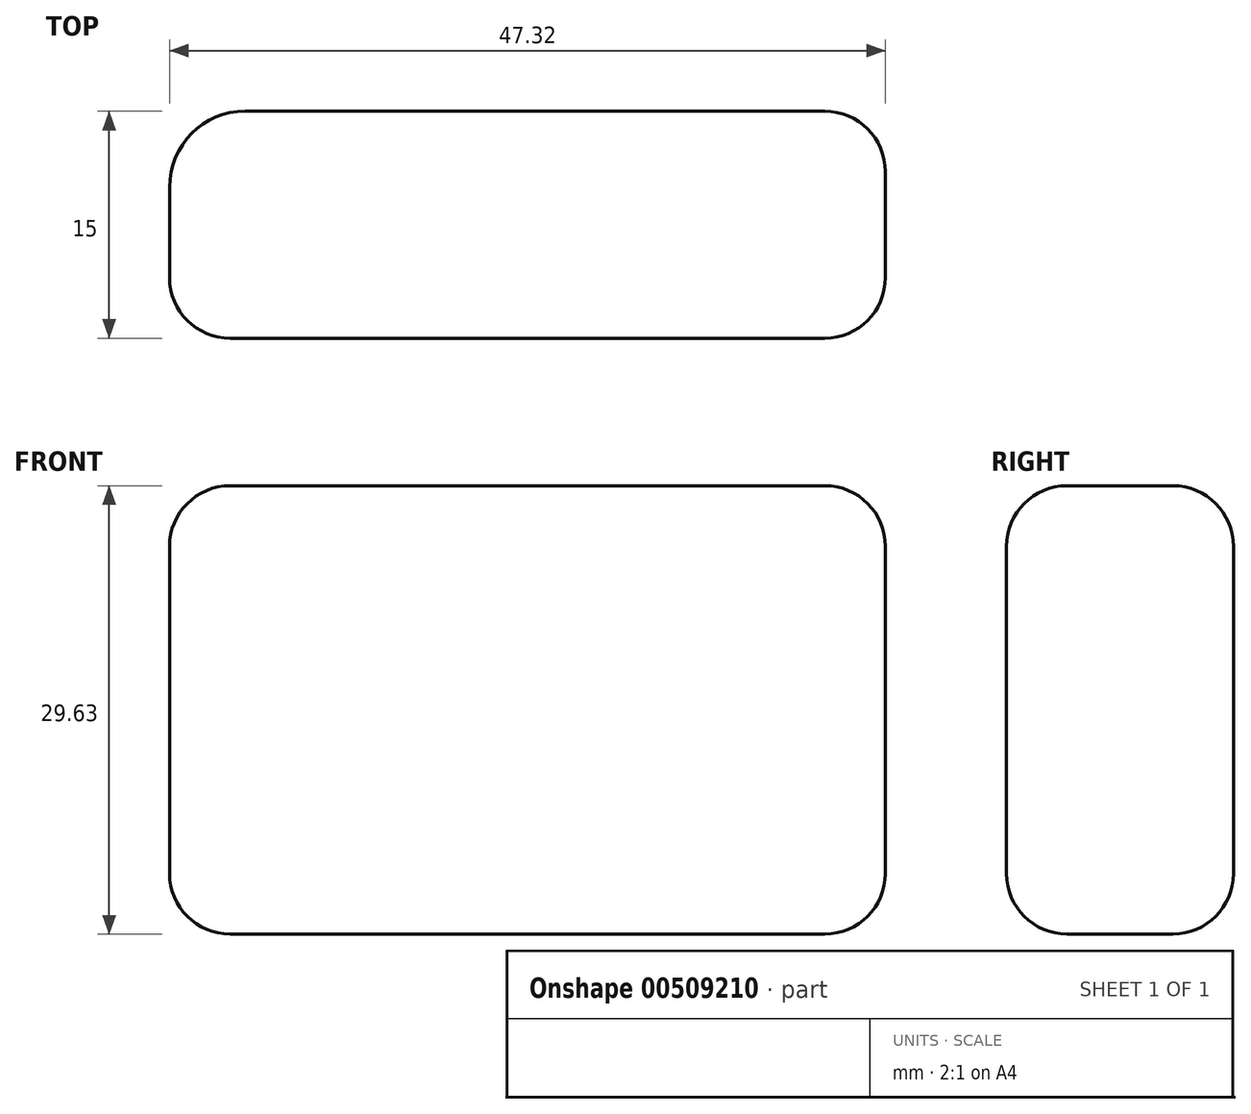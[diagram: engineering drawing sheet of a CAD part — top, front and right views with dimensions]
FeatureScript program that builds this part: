
annotation { "Feature Type Name" : "Feature", "Feature Type Description" : "" }
export const myFeature = defineFeature(function(context is Context, id is Id, definition is map)
    precondition{}
    {
        {
            var Q0;
            Q0=qCreatedBy(makeId("Front.planeOp"),FACE);
            var sketch = newSketch(context, id + "F0", { "sketchPlane" : qUnion([Q0])});
            skLineSegment(sketch, "E0.bottom", {"start": v(-65.84, 12.9) * mm, "end": v(-18.52, 12.9) * mm});
            skLineSegment(sketch, "E0.top", {"start": v(-65.84, -16.72) * mm, "end": v(-18.52, -16.72) * mm});
            skLineSegment(sketch, "E0.left", {"start": v(-65.84, 12.9) * mm, "end": v(-65.84, -16.72) * mm});
            skLineSegment(sketch, "E0.right", {"start": v(-18.52, 12.9) * mm, "end": v(-18.52, -16.72) * mm});
            skSolve(sketch);
        }
        {
            var Q0;
            Q0 = qSketchRegion(id + "F0", true);
            extrude(context, id + "F1", {"entities" : qUnion([Q0]), "depth" : 15 * mm, "offsetDistance" : 25 * mm});
        }
        {
            var Q0;
            Q0=makeQuery(id+"F1.opExtrude","CAP_FACE",FACE,{"disambiguationData":[OSD([sQuery(id+"F0.wireOp",EDGE,"E0.bottom"),sQuery(id+"F0.wireOp",EDGE,"E0.top"),sQuery(id+"F0.wireOp",EDGE,"E0.left"),sQuery(id+"F0.wireOp",EDGE,"E0.right")])],"isStart":false});
            var Q1;
            Q1=makeQuery(id+"F1.opExtrude","SWEPT_EDGE",EDGE,{"disambiguationData":[OSD([sQuery(id+"F0.wireOp",EDGE,"E0.bottom"),sQuery(id+"F0.wireOp",EDGE,"E0.right")])]});
            var Q2;
            Q2=makeQuery(id+"F1.opExtrude","CAP_EDGE",EDGE,{"disambiguationData":[OSD([sQuery(id+"F0.wireOp",EDGE,"E0.bottom")])],"isStart":true});
            var Q3;
            Q3=makeQuery(id+"F1.opExtrude","SWEPT_FACE",FACE,{"disambiguationData":[OSD([sQuery(id+"F0.wireOp",EDGE,"E0.right")])]});
            var Q4;
            Q4=makeQuery(id+"F1.opExtrude","CAP_EDGE",EDGE,{"disambiguationData":[OSD([sQuery(id+"F0.wireOp",EDGE,"E0.top")])],"isStart":true});
            var Q5;
            Q5=makeQuery(id+"F1.opExtrude","SWEPT_EDGE",EDGE,{"disambiguationData":[OSD([sQuery(id+"F0.wireOp",EDGE,"E0.top"),sQuery(id+"F0.wireOp",EDGE,"E0.left")])]});
            var Q6;
            Q6=makeQuery(id+"F1.opExtrude","SWEPT_EDGE",EDGE,{"disambiguationData":[OSD([sQuery(id+"F0.wireOp",EDGE,"E0.bottom"),sQuery(id+"F0.wireOp",EDGE,"E0.left")])]});
            fillet(context, id + "F2", {"entities" : qUnion([Q0, Q1, Q2, Q3, Q4, Q5, Q6]), "radius" : 4 * mm, "tangentPropagation" : true, "allowEdgeOverflow" : false});
        }
        {
            var Q0;
            Q0=makeQuery(id+"F1.opExtrude","CAP_EDGE",EDGE,{"disambiguationData":[OSD([sQuery(id+"F0.wireOp",EDGE,"E0.left")])],"isStart":true});
            fillet(context, id + "F3", {"entities" : qUnion([Q0]), "radius" : 5 * mm, "tangentPropagation" : true, "allowEdgeOverflow" : false});
        }
    });
